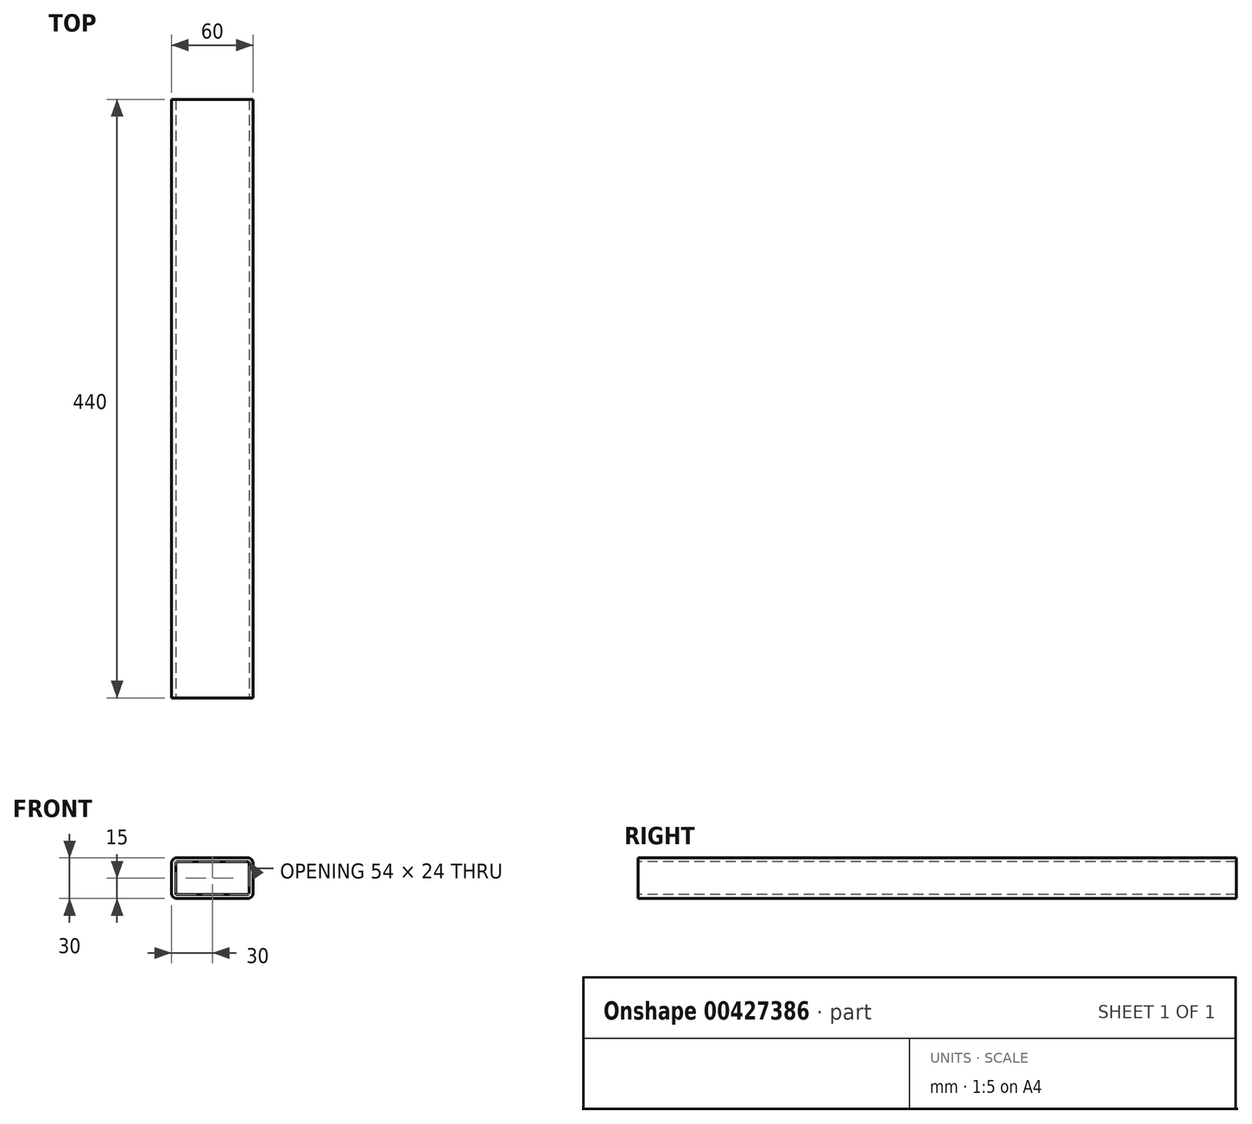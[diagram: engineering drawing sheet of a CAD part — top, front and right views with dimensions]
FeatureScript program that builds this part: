
annotation { "Feature Type Name" : "Feature", "Feature Type Description" : "" }
export const myFeature = defineFeature(function(context is Context, id is Id, definition is map)
    precondition{}
    {
        {
            var Q0;
            Q0=qCreatedBy(makeId("Front.planeOp"),FACE);
            var sketch = newSketch(context, id + "F0", { "sketchPlane" : qUnion([Q0])});
            skLineSegment(sketch, "E0.bottom", {"start": v(26, 15) * mm, "end": v(-26, 15) * mm});
            skLineSegment(sketch, "E0.top", {"start": v(26, -15) * mm, "end": v(-26, -15) * mm});
            skLineSegment(sketch, "E0.left", {"start": v(30, 11) * mm, "end": v(30, -11) * mm});
            skLineSegment(sketch, "E0.right", {"start": v(-30, 11) * mm, "end": v(-30, -11) * mm});
            skPoint(sketch, "E0.middle", {"position": v(0, 0) * mm});
            skPoint(sketch, "E1.visualSharp", {"position": v(-30, 15) * mm});
            skArc(sketch, "E1.filletArc", {"start": v(-26, 15) * mm, "mid": v(-28.83, 13.83) * mm, "end": v(-30, 11) * mm});
            skPoint(sketch, "E2.visualSharp", {"position": v(30, 15) * mm});
            skArc(sketch, "E2.filletArc", {"start": v(30, 11) * mm, "mid": v(28.83, 13.83) * mm, "end": v(26, 15) * mm});
            skPoint(sketch, "E3.visualSharp", {"position": v(30, -15) * mm});
            skArc(sketch, "E3.filletArc", {"start": v(26, -15) * mm, "mid": v(28.83, -13.83) * mm, "end": v(30, -11) * mm});
            skPoint(sketch, "E4.visualSharp", {"position": v(-30, -15) * mm});
            skArc(sketch, "E4.filletArc", {"start": v(-30, -11) * mm, "mid": v(-28.83, -13.83) * mm, "end": v(-26, -15) * mm});
            skArc(sketch, "E5.0", {"start": v(-26, 12) * mm, "mid": v(-26.7, 11.7) * mm, "end": v(-27, 11) * mm});
            skLineSegment(sketch, "E5.1", {"start": v(26, 12) * mm, "end": v(-26, 12) * mm});
            skLineSegment(sketch, "E5.2", {"start": v(-27, 11) * mm, "end": v(-27, -11) * mm});
            skArc(sketch, "E5.3", {"start": v(27, 11) * mm, "mid": v(26.7, 11.7) * mm, "end": v(26, 12) * mm});
            skArc(sketch, "E5.4", {"start": v(-27, -11) * mm, "mid": v(-26.7, -11.7) * mm, "end": v(-26, -12) * mm});
            skLineSegment(sketch, "E5.5", {"start": v(26, -12) * mm, "end": v(-26, -12) * mm});
            skArc(sketch, "E5.6", {"start": v(26, -12) * mm, "mid": v(26.7, -11.7) * mm, "end": v(27, -11) * mm});
            skLineSegment(sketch, "E5.7", {"start": v(27, 11) * mm, "end": v(27, -11) * mm});
            skSolve(sketch);
        }
        {
            var Q0;
            Q0=makeQuery(id+"F0.imprint","IMPRINT",FACE,{"disambiguationData":[TD([[makeQuery(id+"F0.imprint","IMPRINT",EDGE,{"derivedFrom":sQuery(id+"F0.wireOp",EDGE,"E0.bottom")}),1.0]])]});
            extrude(context, id + "F1", {"entities" : qUnion([Q0]), "endBound" : BoundingType.SYMMETRIC, "oppositeDirection" : true, "depth" : (600 - 160) * mm});
        }
    });
